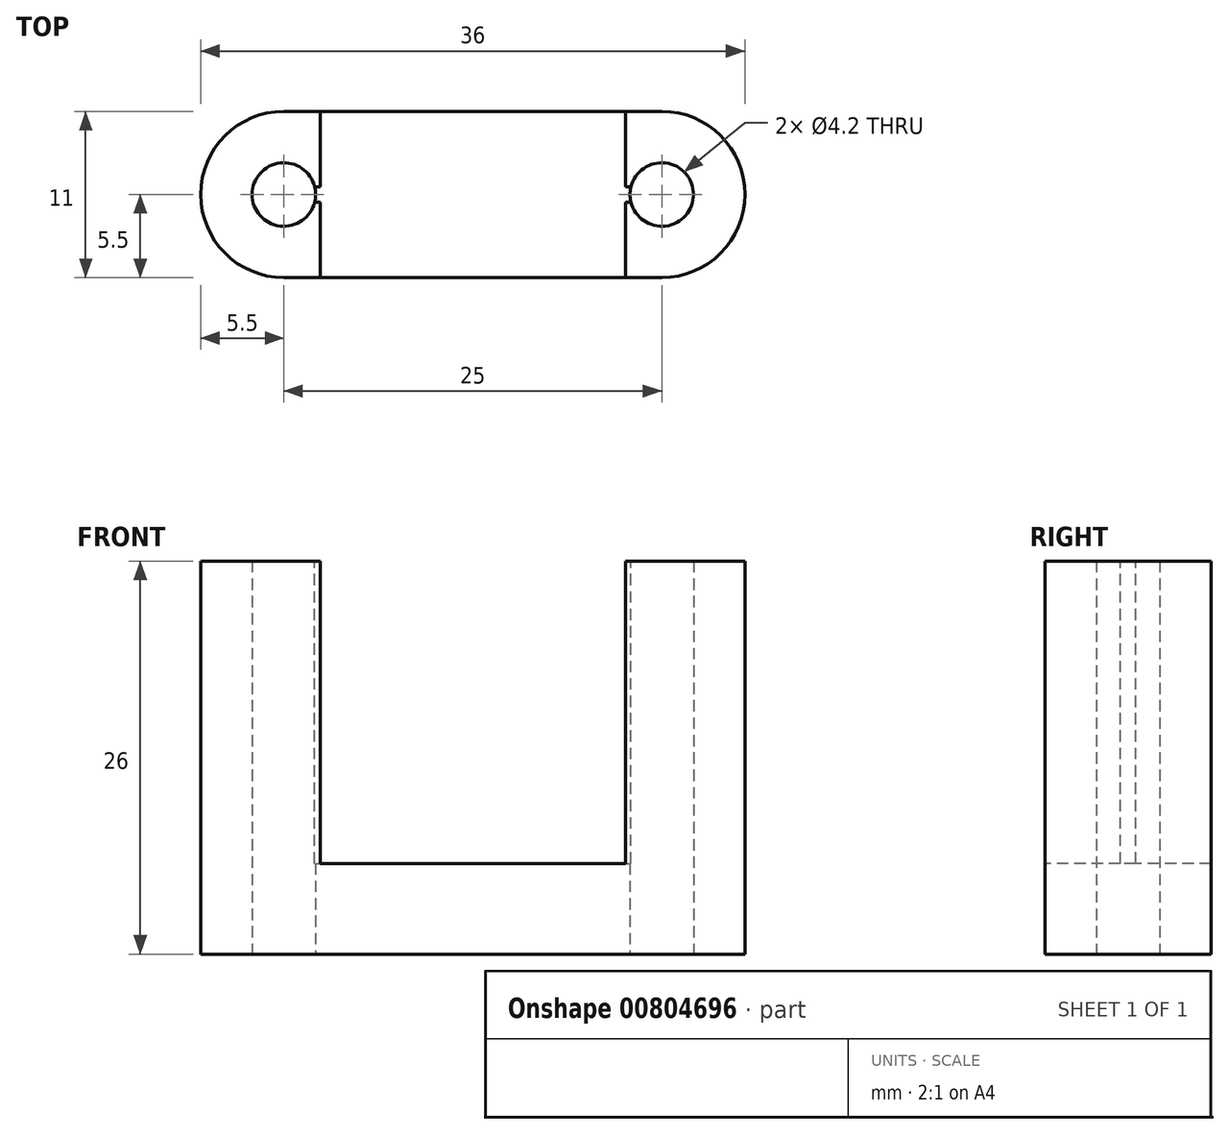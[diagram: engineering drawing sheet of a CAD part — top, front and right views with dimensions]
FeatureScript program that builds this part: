
annotation { "Feature Type Name" : "Feature", "Feature Type Description" : "" }
export const myFeature = defineFeature(function(context is Context, id is Id, definition is map)
    precondition{}
    {
        {
            var Q0;
            Q0=qCreatedBy(makeId("Top.planeOp"),FACE);
            var sketch = newSketch(context, id + "F0", { "sketchPlane" : qUnion([Q0])});
            skLineSegment(sketch, "E0", {"start": v(-12.5, 0) * mm, "end": v(12.5, 0) * mm, "construction": true});
            skArc(sketch, "E1.0.startCap", {"start": v(-12.5, -5.5) * mm, "mid": v(-18, 0) * mm, "end": v(-12.5, 5.5) * mm});
            skArc(sketch, "E1.0.endCap", {"start": v(12.5, 5.5) * mm, "mid": v(18, 0) * mm, "end": v(12.5, -5.5) * mm});
            skLineSegment(sketch, "E1.0.left", {"start": v(-12.5, 5.5) * mm, "end": v(12.5, 5.5) * mm});
            skLineSegment(sketch, "E1.0.right", {"start": v(-12.5, -5.5) * mm, "end": v(12.5, -5.5) * mm});
            skCircle(sketch, "E2", {"center": v(-12.5, 0) * mm, "radius": 2.1 * mm});
            skCircle(sketch, "E3", {"center": v(12.5, 0) * mm, "radius": 2.1 * mm});
            skSolve(sketch);
        }
        {
            var Q0;
            Q0=qSketchRegion(id+"F0",true);
            extrude(context, id + "F1", {"entities" : qUnion([Q0]), "depth" : 26 * mm, "offsetDistance" : 25 * mm});
        }
        {
            var Q0;
            Q0=makeQuery(id+"F1.opExtrude","CAP_FACE",FACE,{"disambiguationData":[OSD([sQuery(id+"F0.wireOp",EDGE,"E1.0.startCap"),sQuery(id+"F0.wireOp",EDGE,"E1.0.endCap"),sQuery(id+"F0.wireOp",EDGE,"E1.0.left"),sQuery(id+"F0.wireOp",EDGE,"E1.0.right"),sQuery(id+"F0.wireOp",EDGE,"E2"),sQuery(id+"F0.wireOp",EDGE,"E3")])],"isStart":false});
            var sketch = newSketch(context, id + "F2", { "sketchPlane" : qUnion([Q0])});
            skLineSegment(sketch, "E4.bottom", {"start": v(-10.1, 5.5) * mm, "end": v(10.1, 5.5) * mm});
            skLineSegment(sketch, "E4.top", {"start": v(-10.1, -5.5) * mm, "end": v(10.1, -5.5) * mm});
            skLineSegment(sketch, "E4.left", {"start": v(-10.1, 5.5) * mm, "end": v(-10.1, 0.5) * mm});
            skLineSegment(sketch, "E4.right", {"start": v(10.1, 5.5) * mm, "end": v(10.1, 0.5) * mm});
            skLineSegment(sketch, "E5.bottom", {"start": v(-10.46, 0.5) * mm, "end": v(-10.1, 0.5) * mm});
            skLineSegment(sketch, "E5.top", {"start": v(-10.46, -0.5) * mm, "end": v(-10.1, -0.5) * mm});
            skLineSegment(sketch, "E5.left", {"start": v(-10.46, 0.5) * mm, "end": v(-10.46, -0.5) * mm});
            skLineSegment(sketch, "E6.bottom", {"start": v(10.1, 0.5) * mm, "end": v(10.46, 0.5) * mm});
            skLineSegment(sketch, "E6.top", {"start": v(10.1, -0.5) * mm, "end": v(10.46, -0.5) * mm});
            skLineSegment(sketch, "E6.right", {"start": v(10.46, 0.5) * mm, "end": v(10.46, -0.5) * mm});
            skLineSegment(sketch, "E7", {"start": v(-10.1, 5.5) * mm, "end": v(10.1, -5.5) * mm, "construction": true});
            skLineSegment(sketch, "E8", {"start": v(0, 0) * mm, "end": v(-10.46, 0) * mm, "construction": true});
            skLineSegment(sketch, "E9.trimOffspring", {"start": v(-10.1, -0.5) * mm, "end": v(-10.1, -5.5) * mm});
            skLineSegment(sketch, "E10.trimOffspring", {"start": v(10.1, -0.5) * mm, "end": v(10.1, -5.5) * mm});
            skSolve(sketch);
        }
        {
            var Q0;
            Q0=qSketchRegion(id+"F2",true);
            extrude(context, id + "F3", {"entities" : qUnion([Q0]), "operationType" : NewBodyOperationType.REMOVE, "oppositeDirection" : true, "depth" : 20 * mm, "offsetDistance" : 25 * mm});
        }
    });
